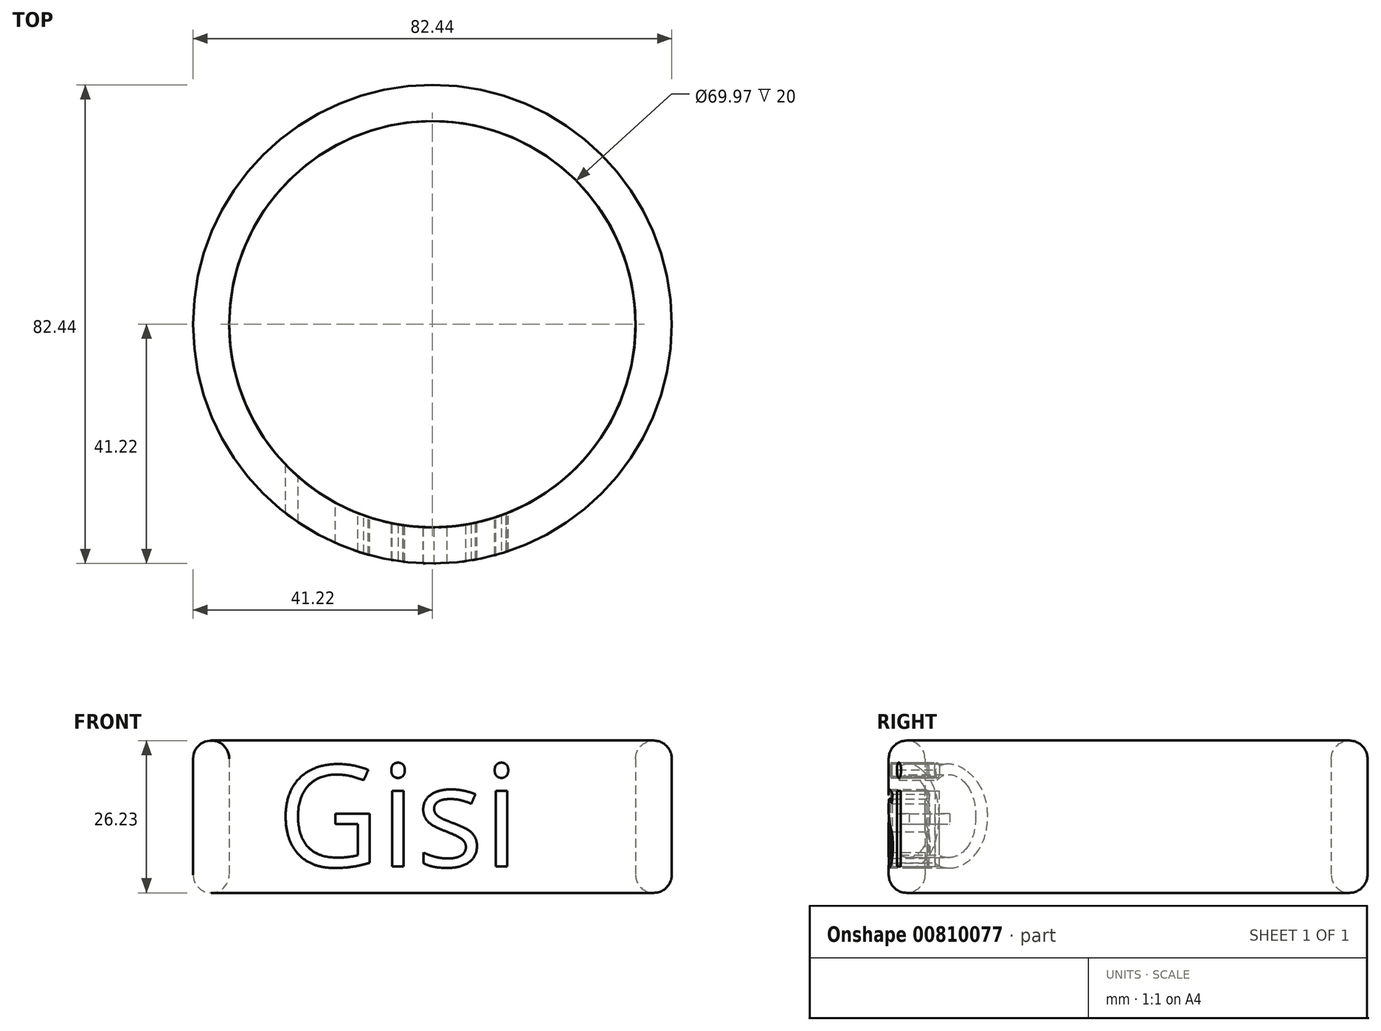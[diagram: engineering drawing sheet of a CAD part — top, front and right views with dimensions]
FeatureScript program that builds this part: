
annotation { "Feature Type Name" : "Feature", "Feature Type Description" : "" }
export const myFeature = defineFeature(function(context is Context, id is Id, definition is map)
    precondition{}
    {
        {
            var Q0;
            Q0=qCreatedBy(makeId("Front.planeOp"),FACE);
            var sketch = newSketch(context, id + "F0", { "sketchPlane" : qUnion([Q0])});
            skLineSegment(sketch, "E0", {"start": v(34.98, 10.23) * mm, "end": v(34.98, -9.77) * mm});
            skLineSegment(sketch, "E1", {"start": v(41.22, 10.23) * mm, "end": v(41.22, -9.77) * mm});
            skArc(sketch, "E2", {"start": v(34.98, -9.77) * mm, "mid": v(38.1, -12.89) * mm, "end": v(41.22, -9.77) * mm});
            skArc(sketch, "E3", {"start": v(34.98, 10.23) * mm, "mid": v(38.1, 13.34) * mm, "end": v(41.22, 10.23) * mm});
            skLineSegment(sketch, "E4", {"start": v(0, -37.32) * mm, "end": v(0, 31.51) * mm});
            skSolve(sketch);
        }
        {
            var Q0;
            Q0=makeQuery(id+"F0.imprint","IMPRINT",FACE,{"disambiguationData":[TD([[makeQuery(id+"F0.imprint","IMPRINT",EDGE,{"derivedFrom":sQuery(id+"F0.wireOp",EDGE,"E0")}),1.0]])]});
            var Q1;
            Q1=sQuery(id+"F0.wireOp",EDGE,"E4");
            revolve(context, id + "F1", {"surfaceOperationType" : NewSurfaceOperationType.NEW, "entities" : qUnion([Q0]), "axis" : qUnion([Q1]), "revolveType" : RevolveType.FULL});
        }
        {
            var Q0;
            Q0=qCreatedBy(makeId("Front.planeOp"),FACE);
            var sketch = newSketch(context, id + "F2", { "sketchPlane" : qUnion([Q0])});
            skText(sketch, "E5", { "text": "Gisi", "fontName": "OpenSans-Regular.ttf"});
            const initialGuessF2  = {"E5": [-0.02677, -0.00836, 1, 0, 0.01756]};
            skSetInitialGuess(sketch, initialGuessF2);
            skSolve(sketch);
        }
        {
            var Q0;
            Q0 = qSketchRegion(id + "F2", true);
            extrude(context, id + "F3", {"entities" : qUnion([Q0]), "operationType" : NewBodyOperationType.REMOVE, "depth" : 107 * mm, "offsetDistance" : 25 * mm});
        }
    });
